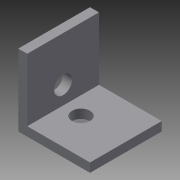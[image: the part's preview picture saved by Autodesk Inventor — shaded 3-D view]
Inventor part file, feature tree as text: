
AUTODESK INVENTOR PART (.ipt)
format: ipt  version: 2014 (Build 180170000, 170)  size: 92,160 bytes
history: native  units: in
note: dims shown in document units (in); Inventor stores cm internally (conversion verified against a paired STEP export)
features: sketch x3, hole x2, extrude x1
ambient origin geometry x8: Origin, YZ Plane, XZ Plane, XY Plane, X Axis, Y Axis, Z Axis, Center Point
bodies: Solid1 (feature_tree)
feature tree (6):
  extrude  "Extrusion1"  Depth=0.125in
  hole  "Hole1"  [1 undecoded]
  hole  "Hole2"  [1 undecoded]
  sketch  "Sketch1"  dims[d0=1.0in d1=0.125in]
  sketch  "Sketch2"  dims[d2=0.875in d3=0.875in]
  sketch  "Sketch3"  dims[d4=0.125in d5=1.0in d6=0.0in d7=0.375in d8=0.25in d9=0.75in d10=0.375in d11=0.25in d12=0.5635in d13=1.0in d14=0.8108in d15=0.375in d16=0.25in d17=0.75in d18=0.375in d19=0.25in d20=0.5635in d21=1.0in d22=0.8108in]
note: 2 required parameter values undecoded (feature->parameter linkage not recoverable at this tier; creation-order binding heuristic only, values carry confidence <= 0.55)
